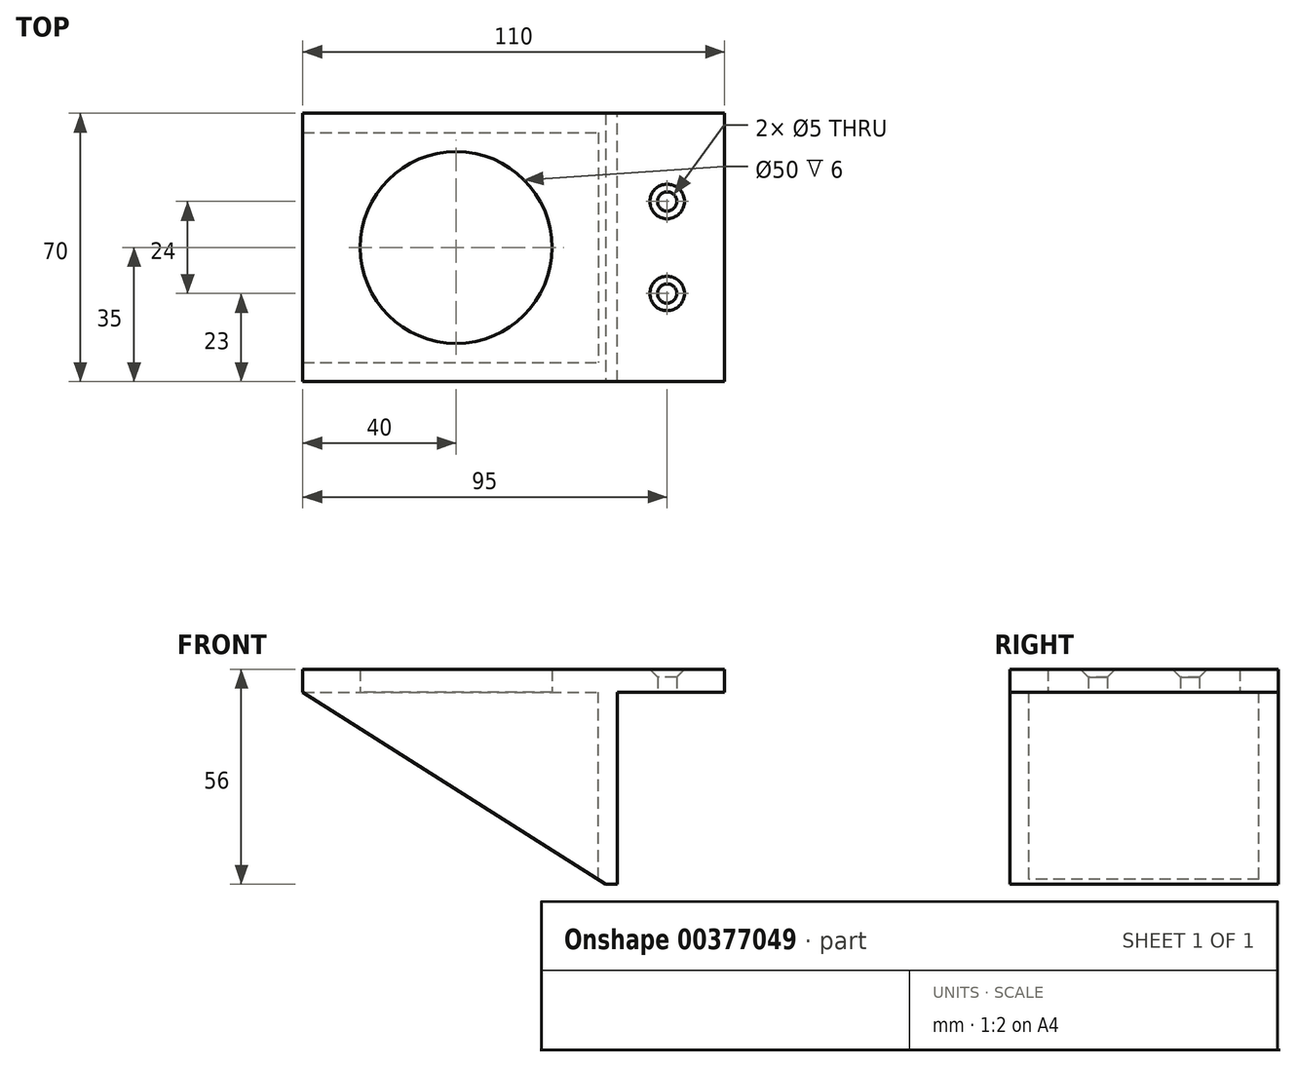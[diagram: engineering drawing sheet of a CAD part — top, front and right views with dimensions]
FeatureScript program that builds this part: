
annotation { "Feature Type Name" : "Feature", "Feature Type Description" : "" }
export const myFeature = defineFeature(function(context is Context, id is Id, definition is map)
    precondition{}
    {
        {
            var Q0;
            Q0=qCreatedBy(makeId("Top.planeOp"),FACE);
            var sketch = newSketch(context, id + "F0", { "sketchPlane" : qUnion([Q0])});
            skLineSegment(sketch, "E0.bottom", {"start": v(55, 35) * mm, "end": v(-55, 35) * mm});
            skLineSegment(sketch, "E0.top", {"start": v(55, -35) * mm, "end": v(-55, -35) * mm});
            skLineSegment(sketch, "E0.left", {"start": v(55, 35) * mm, "end": v(55, -35) * mm});
            skLineSegment(sketch, "E0.right", {"start": v(-55, 35) * mm, "end": v(-55, -35) * mm});
            skPoint(sketch, "E0.middle", {"position": v(0, 0) * mm});
            skLineSegment(sketch, "E1", {"start": v(55, 35) * mm, "end": v(25, 35) * mm, "construction": true});
            skLineSegment(sketch, "E2", {"start": v(25, 35) * mm, "end": v(25, -35) * mm, "construction": true});
            skLineSegment(sketch, "E3", {"start": v(25, 35) * mm, "end": v(-55, -35) * mm, "construction": true});
            skLineSegment(sketch, "E4", {"start": v(-55, 35) * mm, "end": v(25, -35) * mm, "construction": true});
            skCircle(sketch, "E5", {"center": v(-15, 0) * mm, "radius": 25 * mm});
            skLineSegment(sketch, "E6", {"start": v(40, 35) * mm, "end": v(40, 12) * mm, "construction": true});
            skLineSegment(sketch, "E7", {"start": v(40, 12) * mm, "end": v(40, -12) * mm, "construction": true});
            skLineSegment(sketch, "E8", {"start": v(40, -12) * mm, "end": v(40, -35) * mm, "construction": true});
            skCircle(sketch, "E9", {"center": v(40, 12) * mm, "radius": 2.5 * mm});
            skCircle(sketch, "E10", {"center": v(40, -12) * mm, "radius": 2.5 * mm});
            skSolve(sketch);
        }
        {
            var Q0;
            Q0=makeQuery(id+"F0.imprint","IMPRINT",FACE,{"disambiguationData":[TD([[makeQuery(id+"F0.imprint","IMPRINT",EDGE,{"derivedFrom":sQuery(id+"F0.wireOp",EDGE,"E0.bottom")}),1.0]])]});
            extrude(context, id + "F1", {"entities" : qUnion([Q0]), "depth" : 6 * mm});
        }
        {
            var Q0;
            Q0=makeQuery(id+"F1.opExtrude","CAP_FACE",FACE,{"disambiguationData":[OSD([sQuery(id+"F0.wireOp",EDGE,"E0.bottom"),sQuery(id+"F0.wireOp",EDGE,"E0.top"),sQuery(id+"F0.wireOp",EDGE,"E0.left"),sQuery(id+"F0.wireOp",EDGE,"E0.right"),sQuery(id+"F0.wireOp",EDGE,"E5")])],"isStart":true});
            var sketch = newSketch(context, id + "F2", { "sketchPlane" : qUnion([Q0])});
            skLineSegment(sketch, "E11", {"start": v(55, 35) * mm, "end": v(27, 35) * mm, "construction": true});
            skLineSegment(sketch, "E12", {"start": v(27, 35) * mm, "end": v(27, -35) * mm});
            skLineSegment(sketch, "E13", {"start": v(27, -35) * mm, "end": v(22, -35) * mm});
            skLineSegment(sketch, "E14", {"start": v(22, -35) * mm, "end": v(22, 35) * mm});
            skLineSegment(sketch, "E15", {"start": v(22, 35) * mm, "end": v(27, 35) * mm});
            skSolve(sketch);
        }
        {
            var Q0;
            Q0=makeQuery(id+"F2.imprint","IMPRINT",FACE,{"disambiguationData":[TD([[makeQuery(id+"F2.imprint","IMPRINT",EDGE,{"derivedFrom":sQuery(id+"F2.wireOp",EDGE,"E12")}),-1.0]])]});
            extrude(context, id + "F3", {"entities" : qUnion([Q0]), "operationType" : NewBodyOperationType.ADD, "depth" : 50 * mm});
        }
        {
            var Q0;
            {var subQ0=sQuery(id+"F0.wireOp",EDGE,"E5");var subQ1=sQuery(id+"F0.wireOp",EDGE,"E0.top");var subQ2=sQuery(id+"F0.wireOp",EDGE,"E0.right");var subQ3=sQuery(id+"F0.wireOp",EDGE,"E0.bottom");Q0=makeQuery(id+"F3.boolean.opBoolean","SPLIT",FACE,{"disambiguationData":[TD([makeQuery(id+"F1.opExtrude","SWEPT_FACE",FACE,{"disambiguationData":[OSD([subQ2])]})])],"derivedFrom":makeQuery(id+"F1.opExtrude","CAP_FACE",FACE,{"disambiguationData":[OSD([subQ3,subQ1,sQuery(id+"F0.wireOp",EDGE,"E0.left"),subQ2,subQ0])],"isStart":true})});}
            var sketch = newSketch(context, id + "F4", { "sketchPlane" : qUnion([Q0])});
            skLineSegment(sketch, "E16", {"start": v(-55, 35) * mm, "end": v(-55, 30) * mm});
            skLineSegment(sketch, "E17", {"start": v(-55, 30) * mm, "end": v(22, 30) * mm});
            skLineSegment(sketch, "E18", {"start": v(22, 30) * mm, "end": v(22, 35) * mm});
            skLineSegment(sketch, "E19", {"start": v(22, 35) * mm, "end": v(-55, 35) * mm});
            skLineSegment(sketch, "E20", {"start": v(-55, -35) * mm, "end": v(-55, -30) * mm});
            skLineSegment(sketch, "E21", {"start": v(-55, -30) * mm, "end": v(22, -30) * mm});
            skLineSegment(sketch, "E22", {"start": v(22, -30) * mm, "end": v(22, -35) * mm});
            skLineSegment(sketch, "E23", {"start": v(22, -35) * mm, "end": v(-55, -35) * mm});
            skSolve(sketch);
        }
        {
            var Q0;
            Q0=makeQuery(id+"F4.imprint","IMPRINT",FACE,{"disambiguationData":[TD([[makeQuery(id+"F4.imprint","IMPRINT",EDGE,{"derivedFrom":sQuery(id+"F4.wireOp",EDGE,"E16")}),-1.0]])]});
            var Q1;
            Q1=makeQuery(id+"F4.imprint","IMPRINT",FACE,{"disambiguationData":[TD([[makeQuery(id+"F4.imprint","IMPRINT",EDGE,{"derivedFrom":sQuery(id+"F4.wireOp",EDGE,"E20")}),-1.0]])]});
            extrude(context, id + "F5", {"entities" : qUnion([Q0, Q1]), "operationType" : NewBodyOperationType.ADD, "depth" : 50 * mm});
        }
        {
            var Q0;
            Q0=makeQuery(id+"F5.boolean.opBoolean","MERGE",FACE,{"derivedFrom":[makeQuery(id+"F3.boolean.opBoolean","MERGE",FACE,{"derivedFrom":[makeQuery(id+"F1.opExtrude","SWEPT_FACE",FACE,{"disambiguationData":[OSD([sQuery(id+"F0.wireOp",EDGE,"E0.top")])]}),makeQuery(id+"F3.opExtrude","SWEPT_FACE",FACE,{"disambiguationData":[OSD([sQuery(id+"F2.wireOp",EDGE,"E15")])]})]}),makeQuery(id+"F5.opExtrude","SWEPT_FACE",FACE,{"disambiguationData":[OSD([sQuery(id+"F4.wireOp",EDGE,"E19")])]})]});
            var sketch = newSketch(context, id + "F6", { "sketchPlane" : qUnion([Q0])});
            skLineSegment(sketch, "E24", {"start": v(27, -50) * mm, "end": v(24, -50) * mm, "construction": true});
            skLineSegment(sketch, "E25", {"start": v(-55, 0) * mm, "end": v(24, -50) * mm});
            skSolve(sketch);
        }
        {
            var Q0;
            {var subQ0=sQuery(id+"F6.wireOp",EDGE,"E25");Q0=makeQuery(id+"F6.imprint","IMPRINT",FACE,{"disambiguationData":[TD([[makeQuery(id+"F6.imprint","IMPRINT",EDGE,{"derivedFrom":subQ0}),-1.0]])]});}
            extrude(context, id + "F7", {"entities" : qUnion([Q0]), "operationType" : NewBodyOperationType.REMOVE, "oppositeDirection" : true, "depth" : 84.5 * mm});
        }
        {
            var Q0;
            Q0=makeQuery(id+"F1.opExtrude","CAP_EDGE",EDGE,{"disambiguationData":[OSD([sQuery(id+"F0.wireOp",EDGE,"E9")])],"isStart":false});
            chamfer(context, id + "F8", {"entities" : qUnion([Q0]), "width" : 2 * mm, "tangentPropagation" : true});
        }
        {
            var Q0;
            Q0=makeQuery(id+"F1.opExtrude","CAP_EDGE",EDGE,{"disambiguationData":[OSD([sQuery(id+"F0.wireOp",EDGE,"E10")])],"isStart":false});
            chamfer(context, id + "F9", {"entities" : qUnion([Q0]), "width" : 2 * mm, "tangentPropagation" : true});
        }
    });
